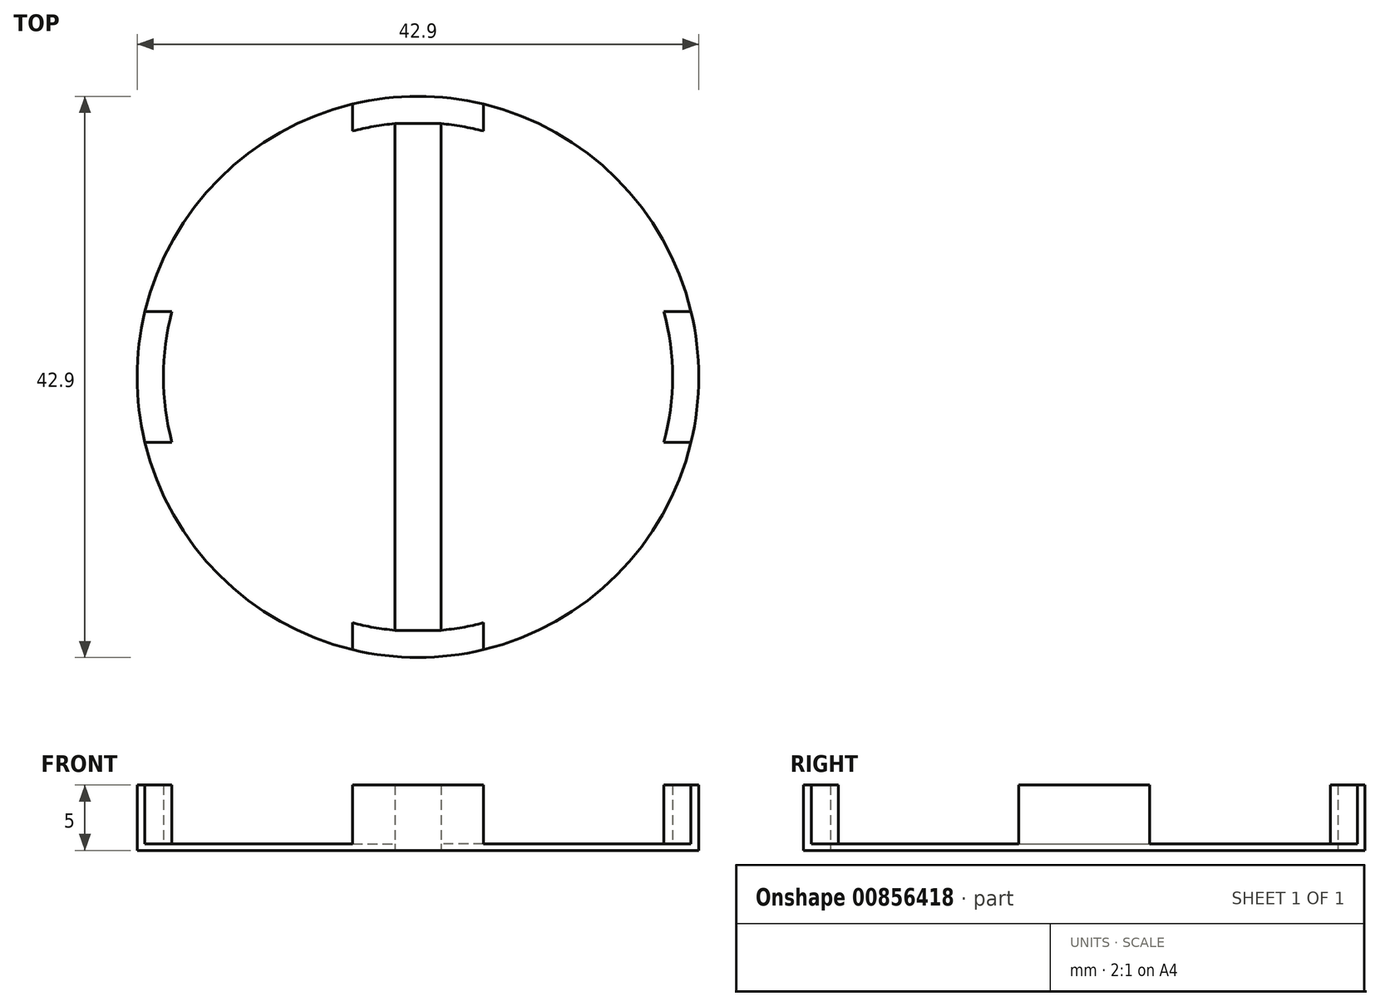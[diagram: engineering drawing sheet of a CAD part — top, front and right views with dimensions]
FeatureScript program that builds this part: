
annotation { "Feature Type Name" : "Feature", "Feature Type Description" : "" }
export const myFeature = defineFeature(function(context is Context, id is Id, definition is map)
    precondition{}
    {
        {
            var Q0;
            Q0=qCreatedBy(makeId("Top.planeOp"),FACE);
            var sketch = newSketch(context, id + "F0", { "sketchPlane" : qUnion([Q0])});
            skArc(sketch, "E0", {"start": v(-1.75, 19.37) * mm, "mid": v(-19.45, 0) * mm, "end": v(-1.75, -19.37) * mm});
            skCircle(sketch, "E1", {"center": v(0, 0) * mm, "radius": 21.45 * mm});
            skLineSegment(sketch, "E2.bottom", {"start": v(5, 20.86) * mm, "end": v(-5, 20.86) * mm});
            skLineSegment(sketch, "E2.top", {"start": v(5, -20.86) * mm, "end": v(-5, -20.86) * mm});
            skLineSegment(sketch, "E2.left", {"start": v(5, 20.86) * mm, "end": v(5, -20.86) * mm});
            skLineSegment(sketch, "E2.right", {"start": v(-5, 20.86) * mm, "end": v(-5, -20.86) * mm});
            skLineSegment(sketch, "E3.bottom", {"start": v(20.86, 5) * mm, "end": v(-20.86, 5) * mm});
            skLineSegment(sketch, "E3.top", {"start": v(20.86, -5) * mm, "end": v(-20.86, -5) * mm});
            skLineSegment(sketch, "E3.left", {"start": v(20.86, 5) * mm, "end": v(20.86, -5) * mm});
            skLineSegment(sketch, "E3.right", {"start": v(-20.86, 5) * mm, "end": v(-20.86, -5) * mm});
            skLineSegment(sketch, "E4.bottom", {"start": v(1.75, -21.38) * mm, "end": v(-1.75, -21.38) * mm});
            skLineSegment(sketch, "E4.top", {"start": v(1.75, 21.38) * mm, "end": v(-1.75, 21.38) * mm});
            skLineSegment(sketch, "E4.left", {"start": v(1.75, -21.38) * mm, "end": v(1.75, 21.38) * mm});
            skLineSegment(sketch, "E4.right", {"start": v(-1.75, -21.38) * mm, "end": v(-1.75, 21.38) * mm});
            skArc(sketch, "E5.trimOffspring", {"start": v(1.75, -19.37) * mm, "mid": v(19.45, 0) * mm, "end": v(1.75, 19.37) * mm});
            skLineSegment(sketch, "E6", {"start": v(1.75, -19.37) * mm, "end": v(-1.75, -19.37) * mm});
            skLineSegment(sketch, "E7", {"start": v(1.75, 19.37) * mm, "end": v(-1.75, 19.37) * mm});
            skSolve(sketch);
        }
        {
            var Q0;
            Q0 = qSketchRegion(id + "F0", true);
            var Q1;
            {var subQ0=sQuery(id+"F0.wireOp",EDGE,"E2.right");var subQ1=sQuery(id+"F0.wireOp",EDGE,"E0");var subQ2=makeQuery(id+"F0.imprint","INTERSECT",VERTEX,{"disambiguationData":[OD(0.0)],"derivedFrom":[subQ1,subQ0]});Q1=makeQuery(id+"F0.imprint","IMPRINT",FACE,{"disambiguationData":[TD([[makeQuery(id+"F0.imprint","IMPRINT",EDGE,{"disambiguationData":[TD([[subQ2,-1.0]])],"derivedFrom":subQ1}),1.0]])]});}
            var Q2;
            {var subQ0=sQuery(id+"F0.wireOp",EDGE,"E2.left");var subQ1=sQuery(id+"F0.wireOp",EDGE,"E0");var subQ2=makeQuery(id+"F0.imprint","INTERSECT",VERTEX,{"disambiguationData":[OD(0.0)],"derivedFrom":[subQ1,subQ0]});Q2=makeQuery(id+"F0.imprint","IMPRINT",FACE,{"disambiguationData":[TD([[makeQuery(id+"F0.imprint","IMPRINT",EDGE,{"disambiguationData":[TD([[subQ2,-1.0]])],"derivedFrom":subQ1}),1.0]])]});}
            var Q3;
            {var subQ0=sQuery(id+"F0.wireOp",EDGE,"E2.left");var subQ1=sQuery(id+"F0.wireOp",EDGE,"E0");var subQ2=makeQuery(id+"F0.imprint","INTERSECT",VERTEX,{"disambiguationData":[OD(0.0)],"derivedFrom":[subQ1,subQ0]});Q3=makeQuery(id+"F0.imprint","IMPRINT",FACE,{"disambiguationData":[TD([[makeQuery(id+"F0.imprint","IMPRINT",EDGE,{"disambiguationData":[TD([[subQ2,1.0]])],"derivedFrom":subQ1}),1.0]])]});}
            var Q4;
            {var subQ0=sQuery(id+"F0.wireOp",EDGE,"E3.bottom");var subQ1=sQuery(id+"F0.wireOp",EDGE,"E2.left");var subQ2=makeQuery(id+"F0.imprint","INTERSECT",VERTEX,{"derivedFrom":[subQ1,subQ0]});Q4=makeQuery(id+"F0.imprint","IMPRINT",FACE,{"disambiguationData":[TD([[makeQuery(id+"F0.imprint","IMPRINT",EDGE,{"disambiguationData":[TD([[subQ2,-1.0]])],"derivedFrom":subQ1}),-1.0]])]});}
            var Q5;
            {var subQ0=sQuery(id+"F0.wireOp",EDGE,"E3.bottom");var subQ1=sQuery(id+"F0.wireOp",EDGE,"E0");var subQ2=makeQuery(id+"F0.imprint","INTERSECT",VERTEX,{"disambiguationData":[OD(0.0)],"derivedFrom":[subQ1,subQ0]});Q5=makeQuery(id+"F0.imprint","IMPRINT",FACE,{"disambiguationData":[TD([[makeQuery(id+"F0.imprint","IMPRINT",EDGE,{"disambiguationData":[TD([[subQ2,1.0]])],"derivedFrom":subQ1}),1.0]])]});}
            var Q6;
            {var subQ0=sQuery(id+"F0.wireOp",EDGE,"E3.bottom");var subQ1=sQuery(id+"F0.wireOp",EDGE,"E0");var subQ2=makeQuery(id+"F0.imprint","INTERSECT",VERTEX,{"disambiguationData":[OD(1.0)],"derivedFrom":[subQ1,subQ0]});Q6=makeQuery(id+"F0.imprint","IMPRINT",FACE,{"disambiguationData":[TD([[makeQuery(id+"F0.imprint","IMPRINT",EDGE,{"disambiguationData":[TD([[subQ2,-1.0]])],"derivedFrom":subQ1}),1.0]])]});}
            var Q7;
            {var subQ0=sQuery(id+"F0.wireOp",EDGE,"E3.top");var subQ1=sQuery(id+"F0.wireOp",EDGE,"E0");var subQ2=makeQuery(id+"F0.imprint","INTERSECT",VERTEX,{"disambiguationData":[OD(0.0)],"derivedFrom":[subQ1,subQ0]});Q7=makeQuery(id+"F0.imprint","IMPRINT",FACE,{"disambiguationData":[TD([[makeQuery(id+"F0.imprint","IMPRINT",EDGE,{"disambiguationData":[TD([[subQ2,-1.0]])],"derivedFrom":subQ1}),1.0]])]});}
            var Q8;
            {var subQ0=sQuery(id+"F0.wireOp",EDGE,"E2.right");var subQ1=sQuery(id+"F0.wireOp",EDGE,"E0");var subQ2=makeQuery(id+"F0.imprint","INTERSECT",VERTEX,{"disambiguationData":[OD(1.0)],"derivedFrom":[subQ1,subQ0]});Q8=makeQuery(id+"F0.imprint","IMPRINT",FACE,{"disambiguationData":[TD([[makeQuery(id+"F0.imprint","IMPRINT",EDGE,{"disambiguationData":[TD([[subQ2,-1.0]])],"derivedFrom":subQ1}),1.0]])]});}
            var Q9;
            {var subQ0=sQuery(id+"F0.wireOp",EDGE,"E2.left");var subQ1=sQuery(id+"F0.wireOp",EDGE,"E0");var subQ2=makeQuery(id+"F0.imprint","INTERSECT",VERTEX,{"disambiguationData":[OD(1.0)],"derivedFrom":[subQ1,subQ0]});Q9=makeQuery(id+"F0.imprint","IMPRINT",FACE,{"disambiguationData":[TD([[makeQuery(id+"F0.imprint","IMPRINT",EDGE,{"disambiguationData":[TD([[subQ2,-1.0]])],"derivedFrom":subQ1}),1.0]])]});}
            var Q10;
            {var subQ0=sQuery(id+"F0.wireOp",EDGE,"E4.right");var subQ1=sQuery(id+"F0.wireOp",EDGE,"E0");var subQ2=makeQuery(id+"F0.imprint","INTERSECT",VERTEX,{"disambiguationData":[OD(0.0)],"derivedFrom":[subQ1,subQ0]});Q10=makeQuery(id+"F0.imprint","IMPRINT",FACE,{"disambiguationData":[TD([[makeQuery(id+"F0.imprint","IMPRINT",EDGE,{"disambiguationData":[TD([[subQ2,-1.0]])],"derivedFrom":subQ1}),1.0]])]});}
            var Q11;
            {var subQ0=sQuery(id+"F0.wireOp",EDGE,"E3.bottom");var subQ1=sQuery(id+"F0.wireOp",EDGE,"E2.right");var subQ2=makeQuery(id+"F0.imprint","INTERSECT",VERTEX,{"derivedFrom":[subQ1,subQ0]});Q11=makeQuery(id+"F0.imprint","IMPRINT",FACE,{"disambiguationData":[TD([[makeQuery(id+"F0.imprint","IMPRINT",EDGE,{"disambiguationData":[TD([[subQ2,-1.0]])],"derivedFrom":subQ1}),1.0]])]});}
            var Q12;
            {var subQ0=sQuery(id+"F0.wireOp",EDGE,"E4.left");var subQ1=sQuery(id+"F0.wireOp",EDGE,"E0");var subQ2=makeQuery(id+"F0.imprint","INTERSECT",VERTEX,{"disambiguationData":[OD(1.0)],"derivedFrom":[subQ1,subQ0]});Q12=makeQuery(id+"F0.imprint","IMPRINT",FACE,{"disambiguationData":[TD([[makeQuery(id+"F0.imprint","IMPRINT",EDGE,{"disambiguationData":[TD([[subQ2,-1.0]])],"derivedFrom":subQ1}),1.0]])]});}
            var Q13;
            {var subQ0=sQuery(id+"F0.wireOp",EDGE,"E4.right");var subQ1=sQuery(id+"F0.wireOp",EDGE,"E0");var subQ2=makeQuery(id+"F0.imprint","INTERSECT",VERTEX,{"disambiguationData":[OD(1.0)],"derivedFrom":[subQ1,subQ0]});Q13=makeQuery(id+"F0.imprint","IMPRINT",FACE,{"disambiguationData":[TD([[makeQuery(id+"F0.imprint","IMPRINT",EDGE,{"disambiguationData":[TD([[subQ2,-1.0]])],"derivedFrom":subQ1}),-1.0]])]});}
            var Q14;
            {var subQ0=sQuery(id+"F0.wireOp",EDGE,"E4.left");var subQ1=sQuery(id+"F0.wireOp",EDGE,"E0");var subQ2=makeQuery(id+"F0.imprint","INTERSECT",VERTEX,{"disambiguationData":[OD(0.0)],"derivedFrom":[subQ1,subQ0]});Q14=makeQuery(id+"F0.imprint","IMPRINT",FACE,{"disambiguationData":[TD([[makeQuery(id+"F0.imprint","IMPRINT",EDGE,{"disambiguationData":[TD([[subQ2,-1.0]])],"derivedFrom":subQ1}),-1.0]])]});}
            var Q15;
            {var subQ0=sQuery(id+"F0.wireOp",EDGE,"E3.top");var subQ1=sQuery(id+"F0.wireOp",EDGE,"E2.left");var subQ2=makeQuery(id+"F0.imprint","INTERSECT",VERTEX,{"derivedFrom":[subQ1,subQ0]});Q15=makeQuery(id+"F0.imprint","IMPRINT",FACE,{"disambiguationData":[TD([[makeQuery(id+"F0.imprint","IMPRINT",EDGE,{"disambiguationData":[TD([[subQ2,-1.0]])],"derivedFrom":subQ1}),-1.0]])]});}
            var Q16;
            {var subQ0=sQuery(id+"F0.wireOp",EDGE,"E3.top");var subQ1=sQuery(id+"F0.wireOp",EDGE,"E2.left");var subQ2=makeQuery(id+"F0.imprint","INTERSECT",VERTEX,{"derivedFrom":[subQ1,subQ0]});Q16=makeQuery(id+"F0.imprint","IMPRINT",FACE,{"disambiguationData":[TD([[makeQuery(id+"F0.imprint","IMPRINT",EDGE,{"disambiguationData":[TD([[subQ2,-1.0]])],"derivedFrom":subQ1}),1.0]])]});}
            var Q17;
            {var subQ0=sQuery(id+"F0.wireOp",EDGE,"E3.bottom");var subQ1=sQuery(id+"F0.wireOp",EDGE,"E2.left");var subQ2=makeQuery(id+"F0.imprint","INTERSECT",VERTEX,{"derivedFrom":[subQ1,subQ0]});Q17=makeQuery(id+"F0.imprint","IMPRINT",FACE,{"disambiguationData":[TD([[makeQuery(id+"F0.imprint","IMPRINT",EDGE,{"disambiguationData":[TD([[subQ2,-1.0]])],"derivedFrom":subQ1}),1.0]])]});}
            var Q18;
            {var subQ0=sQuery(id+"F0.wireOp",EDGE,"E5.trimOffspring");var subQ1=sQuery(id+"F0.wireOp",EDGE,"E2.left");var subQ2=makeQuery(id+"F0.imprint","INTERSECT",VERTEX,{"disambiguationData":[OD(0.0)],"derivedFrom":[subQ1,subQ0]});Q18=makeQuery(id+"F0.imprint","IMPRINT",FACE,{"disambiguationData":[TD([[makeQuery(id+"F0.imprint","IMPRINT",EDGE,{"disambiguationData":[TD([[subQ2,-1.0]])],"derivedFrom":subQ1}),1.0]])]});}
            var Q19;
            {var subQ0=sQuery(id+"F0.wireOp",EDGE,"E5.trimOffspring");var subQ1=sQuery(id+"F0.wireOp",EDGE,"E2.left");var subQ2=makeQuery(id+"F0.imprint","INTERSECT",VERTEX,{"disambiguationData":[OD(0.0)],"derivedFrom":[subQ1,subQ0]});Q19=makeQuery(id+"F0.imprint","IMPRINT",FACE,{"disambiguationData":[TD([[makeQuery(id+"F0.imprint","IMPRINT",EDGE,{"disambiguationData":[TD([[subQ2,-1.0]])],"derivedFrom":subQ1}),-1.0]])]});}
            var Q20;
            {var subQ5=sQuery(id+"F0.wireOp",EDGE,"E7");Q20=makeQuery(id+"F0.imprint","IMPRINT",FACE,{"disambiguationData":[TD([[makeQuery(id+"F0.imprint","IMPRINT",EDGE,{"derivedFrom":subQ5}),-1.0]])]});}
            var Q21;
            {var subQ5=sQuery(id+"F0.wireOp",EDGE,"E6");Q21=makeQuery(id+"F0.imprint","IMPRINT",FACE,{"disambiguationData":[TD([[makeQuery(id+"F0.imprint","IMPRINT",EDGE,{"derivedFrom":subQ5}),1.0]])]});}
            extrude(context, id + "F1", {"entities" : qUnion([Q0, Q1, Q2, Q3, Q4, Q5, Q6, Q7, Q8, Q9, Q10, Q11, Q12, Q13, Q14, Q15, Q16, Q17, Q18, Q19, Q20, Q21]), "depth" : 0.5 * mm, "offsetDistance" : 25.4 * mm});
        }
        {
            var Q0;
            {var subQ0=sQuery(id+"F0.wireOp",EDGE,"E2.top");Q0=makeQuery(id+"F0.imprint","IMPRINT",FACE,{"disambiguationData":[TD([[makeQuery(id+"F0.imprint","IMPRINT",EDGE,{"derivedFrom":subQ0}),1.0]])]});}
            var Q1;
            {var subQ5=sQuery(id+"F0.wireOp",EDGE,"E2.top");Q1=makeQuery(id+"F0.imprint","IMPRINT",FACE,{"disambiguationData":[TD([[makeQuery(id+"F0.imprint","IMPRINT",EDGE,{"derivedFrom":subQ5}),-1.0]])]});}
            var Q2;
            {var subQ0=sQuery(id+"F0.wireOp",EDGE,"E3.left");Q2=makeQuery(id+"F0.imprint","IMPRINT",FACE,{"disambiguationData":[TD([[makeQuery(id+"F0.imprint","IMPRINT",EDGE,{"derivedFrom":subQ0}),1.0]])]});}
            var Q3;
            {var subQ5=sQuery(id+"F0.wireOp",EDGE,"E3.left");Q3=makeQuery(id+"F0.imprint","IMPRINT",FACE,{"disambiguationData":[TD([[makeQuery(id+"F0.imprint","IMPRINT",EDGE,{"derivedFrom":subQ5}),-1.0]])]});}
            var Q4;
            {var subQ0=sQuery(id+"F0.wireOp",EDGE,"E2.bottom");Q4=makeQuery(id+"F0.imprint","IMPRINT",FACE,{"disambiguationData":[TD([[makeQuery(id+"F0.imprint","IMPRINT",EDGE,{"derivedFrom":subQ0}),-1.0]])]});}
            var Q5;
            {var subQ5=sQuery(id+"F0.wireOp",EDGE,"E2.bottom");Q5=makeQuery(id+"F0.imprint","IMPRINT",FACE,{"disambiguationData":[TD([[makeQuery(id+"F0.imprint","IMPRINT",EDGE,{"derivedFrom":subQ5}),1.0]])]});}
            var Q6;
            {var subQ0=sQuery(id+"F0.wireOp",EDGE,"E3.right");Q6=makeQuery(id+"F0.imprint","IMPRINT",FACE,{"disambiguationData":[TD([[makeQuery(id+"F0.imprint","IMPRINT",EDGE,{"derivedFrom":subQ0}),-1.0]])]});}
            var Q7;
            {var subQ5=sQuery(id+"F0.wireOp",EDGE,"E3.right");Q7=makeQuery(id+"F0.imprint","IMPRINT",FACE,{"disambiguationData":[TD([[makeQuery(id+"F0.imprint","IMPRINT",EDGE,{"derivedFrom":subQ5}),1.0]])]});}
            extrude(context, id + "F2", {"entities" : qUnion([Q0, Q1, Q2, Q3, Q4, Q5, Q6, Q7]), "operationType" : NewBodyOperationType.ADD, "depth" : 5 * mm, "offsetDistance" : 25.4 * mm});
        }
        {
            var Q0;
            {var subQ2=sQuery(id+"F0.wireOp",EDGE,"E1");var subQ6=sQuery(id+"F0.wireOp",EDGE,"E4.right");var subQ9=sQuery(id+"F0.wireOp",EDGE,"E4.left");var subQ10=sQuery(id+"F0.wireOp",EDGE,"E2.top");Q0=makeQuery(id+"F2.boolean.opBoolean","SPLIT",FACE,{"disambiguationData":[TD([makeQuery(id+"F2.opExtrude","SWEPT_FACE",FACE,{"disambiguationData":[OSD([subQ10])]})])],"derivedFrom":makeQuery(id+"F1.opExtrude","CAP_FACE",FACE,{"disambiguationData":[OSD([subQ2,subQ9,subQ6,sQuery(id+"F0.wireOp",EDGE,"E6"),sQuery(id+"F0.wireOp",EDGE,"E7")])],"isStart":false})});}
            var Q1;
            {var subQ2=sQuery(id+"F0.wireOp",EDGE,"E1");var subQ5=sQuery(id+"F0.wireOp",EDGE,"E2.bottom");var subQ6=sQuery(id+"F0.wireOp",EDGE,"E4.right");var subQ10=sQuery(id+"F0.wireOp",EDGE,"E4.left");Q1=makeQuery(id+"F2.boolean.opBoolean","SPLIT",FACE,{"disambiguationData":[TD([makeQuery(id+"F2.opExtrude","SWEPT_FACE",FACE,{"disambiguationData":[OSD([subQ5])]})])],"derivedFrom":makeQuery(id+"F1.opExtrude","CAP_FACE",FACE,{"disambiguationData":[OSD([subQ2,subQ10,subQ6,sQuery(id+"F0.wireOp",EDGE,"E6"),sQuery(id+"F0.wireOp",EDGE,"E7")])],"isStart":false})});}
            var Q2;
            Q2=makeQuery(id+"F2.opExtrude","CAP_FACE",FACE,{"disambiguationData":[OSD([sQuery(id+"F0.wireOp",EDGE,"E0"),sQuery(id+"F0.wireOp",EDGE,"E1"),sQuery(id+"F0.wireOp",EDGE,"E2.top"),sQuery(id+"F0.wireOp",EDGE,"E2.left"),sQuery(id+"F0.wireOp",EDGE,"E2.right"),sQuery(id+"F0.wireOp",EDGE,"E4.left"),sQuery(id+"F0.wireOp",EDGE,"E4.right"),sQuery(id+"F0.wireOp",EDGE,"E5.trimOffspring"),sQuery(id+"F0.wireOp",EDGE,"E6")])],"isStart":false});
            extrude(context, id + "F3", {"entities" : qUnion([Q0, Q1]), "operationType" : NewBodyOperationType.ADD, "endBound" : BoundingType.UP_TO_SURFACE, "depth" : 25.4 * mm, "endBoundEntityFace" : qUnion([Q2]), "offsetDistance" : 25.4 * mm});
        }
    });
